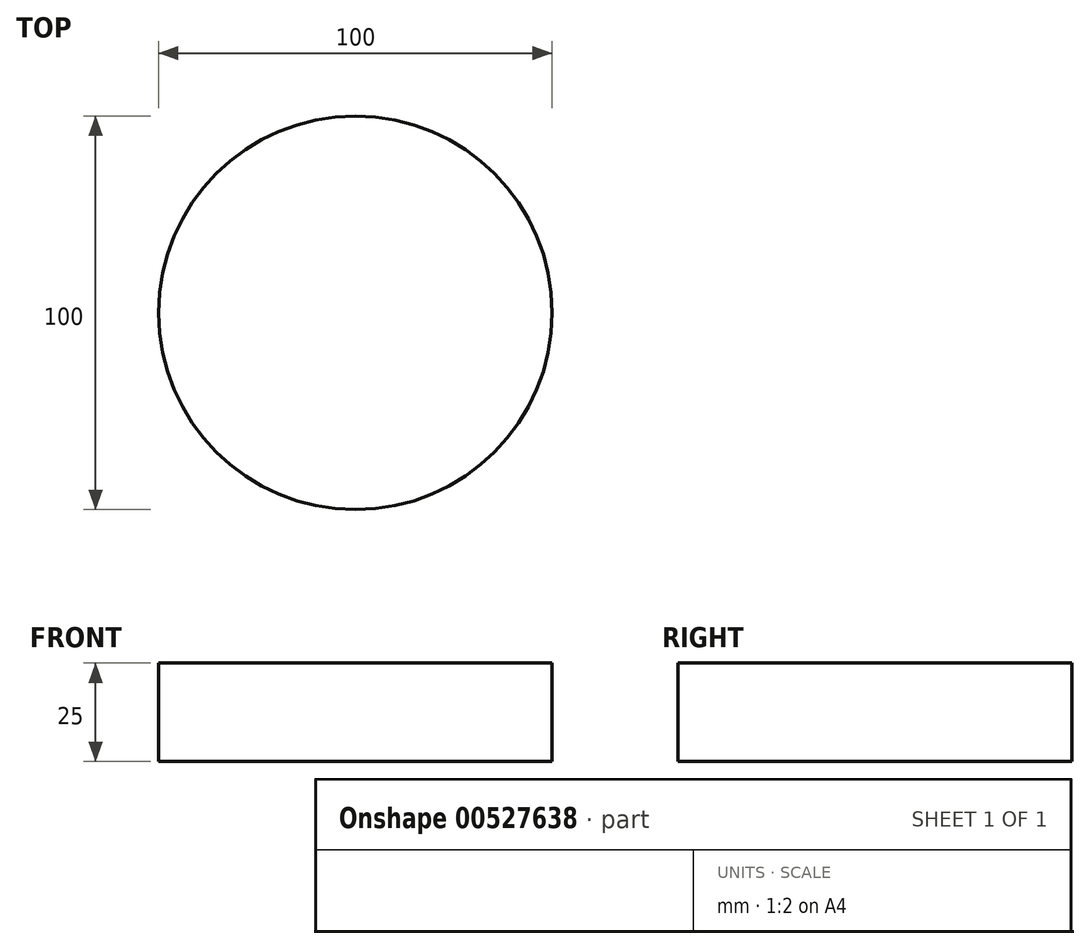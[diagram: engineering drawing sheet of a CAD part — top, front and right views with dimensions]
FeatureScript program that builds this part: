
annotation { "Feature Type Name" : "Feature", "Feature Type Description" : "" }
export const myFeature = defineFeature(function(context is Context, id is Id, definition is map)
    precondition{}
    {
        {
            var Q0;
            Q0=qCreatedBy(makeId("Top.planeOp"),FACE);
            var sketch = newSketch(context, id + "F0", { "sketchPlane" : qUnion([Q0])});
            skCircle(sketch, "E0", {"center": v(0, 0) * mm, "radius": 50 * mm});
            skCircle(sketch, "E1", {"center": v(0, 0) * mm, "radius": 30 * mm});
            skLineSegment(sketch, "E2", {"start": v(0, 68.15) * mm, "end": v(0, 10) * mm, "construction": true});
            skLineSegment(sketch, "E3", {"start": v(3.5, 0) * mm, "end": v(10, 0) * mm});
            skLineSegment(sketch, "E4.MirrorCS", {"start": v(-3.5, 0) * mm, "end": v(-10, 0) * mm});
            skCircle(sketch, "E5", {"center": v(0, 0) * mm, "radius": 10 * mm});
            skCircle(sketch, "E6", {"center": v(-3.62, -3.45) * mm, "radius": 1.5 * mm});
            skCircle(sketch, "E7.MirrorC", {"center": v(3.62, -3.45) * mm, "radius": 1.5 * mm});
            skCircle(sketch, "E8.MirrorC", {"center": v(-3.62, 3.45) * mm, "radius": 1.5 * mm});
            skCircle(sketch, "E9.MirrorC", {"center": v(3.62, 3.45) * mm, "radius": 1.5 * mm});
            skCircle(sketch, "E10", {"center": v(0, 0) * mm, "radius": 3.5 * mm});
            skLineSegment(sketch, "E11.trimOffspring", {"start": v(0, -10) * mm, "end": v(0, -63.6) * mm, "construction": true});
            skSolve(sketch);
        }
        {
            var Q0;
            Q0=sQuery(id+"F0.wireOp",EDGE,"E0");
            extrude(context, id + "F1", {"bodyType" : ToolBodyType.SURFACE, "surfaceEntities" : qUnion([Q0]), "depth" : 25 * mm, "offsetDistance" : 25 * mm});
        }
    });
